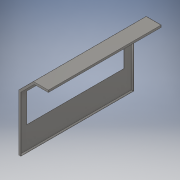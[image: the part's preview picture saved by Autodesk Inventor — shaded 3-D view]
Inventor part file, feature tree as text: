
AUTODESK INVENTOR PART (.ipt)
format: ipt  version: 2018 (Build 220112000, 112)  size: 197,120 bytes
history: native  units: in
note: dims shown in document units (in); Inventor stores cm internally (conversion verified against a paired STEP export)
features: extrude x8, sketch x8, projected_geometry x1
ambient origin geometry x8: Origin, YZ Plane, XZ Plane, XY Plane, X Axis, Y Axis, Z Axis, Center Point
bodies: Solid1 (feature_tree)
feature tree (17):
  extrude  "Extrusion1"  Depth=31.4961in
  extrude  "Extrusion2"  Depth=45.6693in TaperAngle=0.0deg
  extrude  "Extrusion3"  Depth=22.8346in
  extrude  "Extrusion4"  Depth=39.3701in
  extrude  "Extrusion5"  Depth=11.811in
  extrude  "Extrusion6"  Depth=0.063in
  extrude  "Extrusion7"  Depth=0.063in TaperAngle=0.0deg
  extrude  "Extrusion8"  Depth=0.063in TaperAngle=0.0deg
  sketch  "Sketch1"  dims[d0=6.063in d1=31.4961in]
  sketch  "Sketch2"  dims[d2=135.0deg d6=45.6693in d7=0.0in]
  sketch  "Sketch3"  dims[d8=5.9055in d9=22.8346in]
  sketch  "Sketch4"  dims[d10=2.7559in d13=39.3701in]
  projected_geometry  "Projected Loop1"
  sketch  "Sketch5"  dims[d14=11.811in d16=1.9685in]
  sketch  "Sketch6"  dims[d17=47.2441in d18=0.0in d19=0.063in]
  sketch  "Sketch7"  dims[d20=0.7874in d21=0.063in d22=0.0in]
  sketch  "Sketch8"  dims[d23=0.063in d24=0.0in d25=0.063in d26=0.0in d27=0.063in d28=0.0in d32=0.063in d33=0.7874in d34=0.063in d35=0.7874in d36=0.063in d37=0.0in d38=0.7874in d39=0.063in d40=0.7874in d41=0.063in d42=0.063in d43=0.0in]
